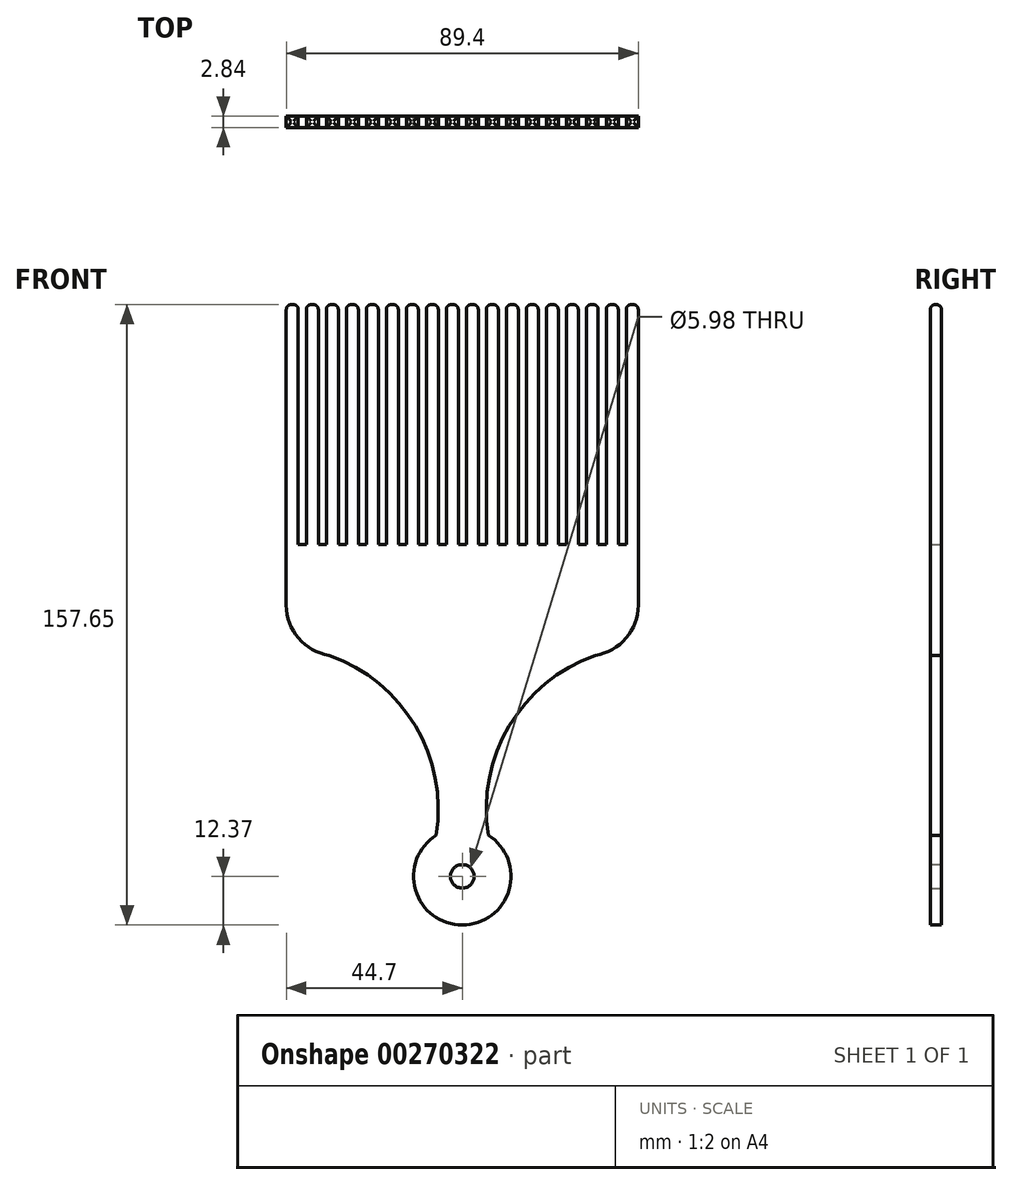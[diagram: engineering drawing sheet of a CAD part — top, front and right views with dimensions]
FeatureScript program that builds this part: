
annotation { "Feature Type Name" : "Feature", "Feature Type Description" : "" }
export const myFeature = defineFeature(function(context is Context, id is Id, definition is map)
    precondition{}
    {
        {
            var Q0;
            Q0=qCreatedBy(makeId("Front.planeOp"),FACE);
            var sketch = newSketch(context, id + "F0", { "sketchPlane" : qUnion([Q0])});
            skLineSegment(sketch, "E0", {"start": v(-55.88, 181.6) * mm, "end": v(-55.88, 86.13) * mm});
            skLineSegment(sketch, "E1", {"start": v(-55.88, 181.6) * mm, "end": v(-52.07, 181.6) * mm});
            skLineSegment(sketch, "E2", {"start": v(-52.07, 181.6) * mm, "end": v(-52.07, 105.4) * mm});
            skArc(sketch, "E3", {"start": v(-55.88, 86.13) * mm, "mid": v(-52, 75.65) * mm, "end": v(-42.24, 70.21) * mm});
            skArc(sketch, "E4", {"start": v(-8.28, 13.06) * mm, "mid": v(-14.9, 47.8) * mm, "end": v(-42.24, 70.21) * mm});
            skArc(sketch, "E5", {"start": v(-8.28, 13.06) * mm, "mid": v(-14.86, -4.31) * mm, "end": v(0, -15.47) * mm});
            skLineSegment(sketch, "E6", {"start": v(-52.07, 105.4) * mm, "end": v(-49.53, 105.4) * mm});
            skLineSegment(sketch, "E7", {"start": v(-49.53, 105.4) * mm, "end": v(-49.53, 181.6) * mm});
            skLineSegment(sketch, "E8", {"start": v(-49.53, 181.6) * mm, "end": v(-45.72, 181.6) * mm});
            skLineSegment(sketch, "E9", {"start": v(-45.72, 181.6) * mm, "end": v(-45.72, 105.4) * mm});
            skLineSegment(sketch, "E10", {"start": v(-45.72, 105.4) * mm, "end": v(-43.18, 105.4) * mm});
            skLineSegment(sketch, "E11", {"start": v(0, -168.17) * mm, "end": v(0, 92.35) * mm, "construction": true});
            skLineSegment(sketch, "E12.MirrorCS", {"start": v(55.88, 181.6) * mm, "end": v(52.07, 181.6) * mm});
            skLineSegment(sketch, "E13.MirrorCS", {"start": v(49.53, 181.6) * mm, "end": v(45.72, 181.6) * mm});
            skLineSegment(sketch, "E14.MirrorCS", {"start": v(45.72, 105.4) * mm, "end": v(43.18, 105.4) * mm});
            skLineSegment(sketch, "E15.MirrorCS", {"start": v(52.07, 105.4) * mm, "end": v(49.53, 105.4) * mm});
            skLineSegment(sketch, "E16.MirrorCS", {"start": v(52.07, 181.6) * mm, "end": v(52.07, 105.4) * mm});
            skArc(sketch, "E17.MirrorCS", {"start": v(8.28, 13.06) * mm, "mid": v(14.86, -4.31) * mm, "end": v(0, -15.47) * mm});
            skLineSegment(sketch, "E18.MirrorCS", {"start": v(45.72, 181.6) * mm, "end": v(45.72, 105.4) * mm});
            skArc(sketch, "E19.MirrorCS", {"start": v(55.88, 86.13) * mm, "mid": v(52, 75.65) * mm, "end": v(42.24, 70.21) * mm});
            skLineSegment(sketch, "E20.MirrorCS", {"start": v(49.53, 105.4) * mm, "end": v(49.53, 181.6) * mm});
            skArc(sketch, "E21.MirrorCS", {"start": v(8.28, 13.06) * mm, "mid": v(14.9, 47.8) * mm, "end": v(42.24, 70.21) * mm});
            skLineSegment(sketch, "E22.MirrorCS", {"start": v(55.88, 181.6) * mm, "end": v(55.88, 86.13) * mm});
            skLineSegment(sketch, "E23.1.0.0", {"start": v(-39.37, 181.6) * mm, "end": v(-39.37, 105.4) * mm});
            skLineSegment(sketch, "E23.1.0.1", {"start": v(-43.18, 105.4) * mm, "end": v(-43.18, 181.6) * mm});
            skLineSegment(sketch, "E23.1.0.2", {"start": v(-39.37, 105.4) * mm, "end": v(-36.83, 105.4) * mm});
            skLineSegment(sketch, "E23.1.0.3", {"start": v(-43.18, 181.6) * mm, "end": v(-39.37, 181.6) * mm});
            skLineSegment(sketch, "E23.2.0.0", {"start": v(-33.02, 181.6) * mm, "end": v(-33.02, 105.4) * mm});
            skLineSegment(sketch, "E23.2.0.1", {"start": v(-36.83, 105.4) * mm, "end": v(-36.83, 181.6) * mm});
            skLineSegment(sketch, "E23.2.0.2", {"start": v(-33.02, 105.4) * mm, "end": v(-30.48, 105.4) * mm});
            skLineSegment(sketch, "E23.2.0.3", {"start": v(-36.83, 181.6) * mm, "end": v(-33.02, 181.6) * mm});
            skLineSegment(sketch, "E23.3.0.0", {"start": v(-26.67, 181.6) * mm, "end": v(-26.67, 105.4) * mm});
            skLineSegment(sketch, "E23.3.0.1", {"start": v(-30.48, 105.4) * mm, "end": v(-30.48, 181.6) * mm});
            skLineSegment(sketch, "E23.3.0.2", {"start": v(-26.67, 105.4) * mm, "end": v(-24.13, 105.4) * mm});
            skLineSegment(sketch, "E23.3.0.3", {"start": v(-30.48, 181.6) * mm, "end": v(-26.67, 181.6) * mm});
            skLineSegment(sketch, "E23.4.0.0", {"start": v(-20.32, 181.6) * mm, "end": v(-20.32, 105.4) * mm});
            skLineSegment(sketch, "E23.4.0.1", {"start": v(-24.13, 105.4) * mm, "end": v(-24.13, 181.6) * mm});
            skLineSegment(sketch, "E23.4.0.2", {"start": v(-20.32, 105.4) * mm, "end": v(-17.78, 105.4) * mm});
            skLineSegment(sketch, "E23.4.0.3", {"start": v(-24.13, 181.6) * mm, "end": v(-20.32, 181.6) * mm});
            skLineSegment(sketch, "E23.5.0.0", {"start": v(-13.97, 181.6) * mm, "end": v(-13.97, 105.4) * mm});
            skLineSegment(sketch, "E23.5.0.1", {"start": v(-17.78, 105.4) * mm, "end": v(-17.78, 181.6) * mm});
            skLineSegment(sketch, "E23.5.0.2", {"start": v(-13.97, 105.4) * mm, "end": v(-11.43, 105.4) * mm});
            skLineSegment(sketch, "E23.5.0.3", {"start": v(-17.78, 181.6) * mm, "end": v(-13.97, 181.6) * mm});
            skLineSegment(sketch, "E23.6.0.0", {"start": v(-7.62, 181.6) * mm, "end": v(-7.62, 105.4) * mm});
            skLineSegment(sketch, "E23.6.0.1", {"start": v(-11.43, 105.4) * mm, "end": v(-11.43, 181.6) * mm});
            skLineSegment(sketch, "E23.6.0.2", {"start": v(-7.62, 105.4) * mm, "end": v(-5.08, 105.4) * mm});
            skLineSegment(sketch, "E23.6.0.3", {"start": v(-11.43, 181.6) * mm, "end": v(-7.62, 181.6) * mm});
            skLineSegment(sketch, "E23.7.0.0", {"start": v(-1.27, 181.6) * mm, "end": v(-1.27, 105.4) * mm});
            skLineSegment(sketch, "E23.7.0.1", {"start": v(-5.08, 105.4) * mm, "end": v(-5.08, 181.6) * mm});
            skLineSegment(sketch, "E23.7.0.2", {"start": v(-1.27, 105.4) * mm, "end": v(1.27, 105.4) * mm});
            skLineSegment(sketch, "E23.7.0.3", {"start": v(-5.08, 181.6) * mm, "end": v(-1.27, 181.6) * mm});
            skLineSegment(sketch, "E23.direction1", {"start": v(-49.53, 105.4) * mm, "end": v(-43.18, 105.4) * mm, "construction": true});
            skLineSegment(sketch, "E24.MirrorCS", {"start": v(11.43, 181.6) * mm, "end": v(7.62, 181.6) * mm});
            skLineSegment(sketch, "E25.MirrorCS", {"start": v(20.32, 105.4) * mm, "end": v(17.78, 105.4) * mm});
            skLineSegment(sketch, "E26.MirrorCS", {"start": v(7.62, 105.4) * mm, "end": v(5.08, 105.4) * mm});
            skLineSegment(sketch, "E27.MirrorCS", {"start": v(17.78, 181.6) * mm, "end": v(13.97, 181.6) * mm});
            skLineSegment(sketch, "E28.MirrorCS", {"start": v(30.48, 181.6) * mm, "end": v(26.67, 181.6) * mm});
            skLineSegment(sketch, "E29.MirrorCS", {"start": v(26.67, 105.4) * mm, "end": v(24.13, 105.4) * mm});
            skLineSegment(sketch, "E30.MirrorCS", {"start": v(13.97, 105.4) * mm, "end": v(11.43, 105.4) * mm});
            skLineSegment(sketch, "E31.MirrorCS", {"start": v(24.13, 181.6) * mm, "end": v(20.32, 181.6) * mm});
            skLineSegment(sketch, "E32.MirrorCS", {"start": v(39.37, 105.4) * mm, "end": v(36.83, 105.4) * mm});
            skLineSegment(sketch, "E33.MirrorCS", {"start": v(33.02, 105.4) * mm, "end": v(30.48, 105.4) * mm});
            skLineSegment(sketch, "E34.MirrorCS", {"start": v(5.08, 181.6) * mm, "end": v(1.27, 181.6) * mm});
            skLineSegment(sketch, "E35.MirrorCS", {"start": v(1.27, 105.4) * mm, "end": v(-1.27, 105.4) * mm});
            skLineSegment(sketch, "E36.MirrorCS", {"start": v(1.27, 181.6) * mm, "end": v(1.27, 105.4) * mm});
            skLineSegment(sketch, "E37.MirrorCS", {"start": v(17.78, 105.4) * mm, "end": v(17.78, 181.6) * mm});
            skLineSegment(sketch, "E38.MirrorCS", {"start": v(36.83, 181.6) * mm, "end": v(33.02, 181.6) * mm});
            skLineSegment(sketch, "E39.MirrorCS", {"start": v(5.08, 105.4) * mm, "end": v(5.08, 181.6) * mm});
            skLineSegment(sketch, "E40.MirrorCS", {"start": v(26.67, 181.6) * mm, "end": v(26.67, 105.4) * mm});
            skLineSegment(sketch, "E41.MirrorCS", {"start": v(39.37, 181.6) * mm, "end": v(39.37, 105.4) * mm});
            skLineSegment(sketch, "E42.MirrorCS", {"start": v(13.97, 181.6) * mm, "end": v(13.97, 105.4) * mm});
            skLineSegment(sketch, "E43.MirrorCS", {"start": v(43.18, 105.4) * mm, "end": v(43.18, 181.6) * mm});
            skLineSegment(sketch, "E44.MirrorCS", {"start": v(30.48, 105.4) * mm, "end": v(30.48, 181.6) * mm});
            skLineSegment(sketch, "E45.MirrorCS", {"start": v(43.18, 181.6) * mm, "end": v(39.37, 181.6) * mm});
            skLineSegment(sketch, "E46.MirrorCS", {"start": v(49.53, 105.4) * mm, "end": v(43.18, 105.4) * mm, "construction": true});
            skLineSegment(sketch, "E47.MirrorCS", {"start": v(11.43, 105.4) * mm, "end": v(11.43, 181.6) * mm});
            skLineSegment(sketch, "E48.MirrorCS", {"start": v(33.02, 181.6) * mm, "end": v(33.02, 105.4) * mm});
            skLineSegment(sketch, "E49.MirrorCS", {"start": v(36.83, 105.4) * mm, "end": v(36.83, 181.6) * mm});
            skLineSegment(sketch, "E50.MirrorCS", {"start": v(24.13, 105.4) * mm, "end": v(24.13, 181.6) * mm});
            skLineSegment(sketch, "E51.MirrorCS", {"start": v(7.62, 181.6) * mm, "end": v(7.62, 105.4) * mm});
            skLineSegment(sketch, "E52.MirrorCS", {"start": v(20.32, 181.6) * mm, "end": v(20.32, 105.4) * mm});
            skCircle(sketch, "E53", {"center": v(0, 0) * mm, "radius": 3.74 * mm});
            skSolve(sketch);
        }
        {
            var Q0;
            Q0 = qSketchRegion(id + "F0", true);
            extrude(context, id + "F1", {"entities" : qUnion([Q0]), "depth" : 3.56 * mm});
        }
        {
            var Q0;
            Q0=qCreatedBy(makeId("Front.planeOp"),FACE);
            cPlane(context, id + "F2", {"entities" : qUnion([Q0]), "cplaneType" : CPlaneType.OFFSET, "offset" : 1.27 * mm, "width" : 152.4 * mm, "height" : 152.4 * mm});
        }
        {
            var Q0;
            Q0=makeQuery(id+"F1.opExtrude","SWEPT_BODY",BODY,{"disambiguationData":[OSD([sQuery(id+"F0.wireOp",EDGE,"E0"),sQuery(id+"F0.wireOp",EDGE,"E1"),sQuery(id+"F0.wireOp",EDGE,"E2"),sQuery(id+"F0.wireOp",EDGE,"E3"),sQuery(id+"F0.wireOp",EDGE,"E4"),sQuery(id+"F0.wireOp",EDGE,"E5"),sQuery(id+"F0.wireOp",EDGE,"E6"),sQuery(id+"F0.wireOp",EDGE,"E7"),sQuery(id+"F0.wireOp",EDGE,"E8"),sQuery(id+"F0.wireOp",EDGE,"E9"),sQuery(id+"F0.wireOp",EDGE,"E10"),sQuery(id+"F0.wireOp",EDGE,"E12.MirrorCS"),sQuery(id+"F0.wireOp",EDGE,"E15.MirrorCS"),sQuery(id+"F0.wireOp",EDGE,"E16.MirrorCS"),sQuery(id+"F0.wireOp",EDGE,"E17.MirrorCS"),sQuery(id+"F0.wireOp",EDGE,"E19.MirrorCS"),sQuery(id+"F0.wireOp",EDGE,"E21.MirrorCS"),sQuery(id+"F0.wireOp",EDGE,"E22.MirrorCS"),sQuery(id+"F0.wireOp",EDGE,"E23.1.0.0"),sQuery(id+"F0.wireOp",EDGE,"E23.1.0.1"),sQuery(id+"F0.wireOp",EDGE,"E23.1.0.2"),sQuery(id+"F0.wireOp",EDGE,"E23.1.0.3"),sQuery(id+"F0.wireOp",EDGE,"E23.2.0.0"),sQuery(id+"F0.wireOp",EDGE,"E23.2.0.1"),sQuery(id+"F0.wireOp",EDGE,"E23.2.0.2"),sQuery(id+"F0.wireOp",EDGE,"E23.2.0.3"),sQuery(id+"F0.wireOp",EDGE,"E23.3.0.0"),sQuery(id+"F0.wireOp",EDGE,"E23.3.0.1"),sQuery(id+"F0.wireOp",EDGE,"E23.3.0.2"),sQuery(id+"F0.wireOp",EDGE,"E23.3.0.3"),sQuery(id+"F0.wireOp",EDGE,"E23.4.0.0"),sQuery(id+"F0.wireOp",EDGE,"E23.4.0.1"),sQuery(id+"F0.wireOp",EDGE,"E23.4.0.2"),sQuery(id+"F0.wireOp",EDGE,"E23.4.0.3"),sQuery(id+"F0.wireOp",EDGE,"E23.5.0.0"),sQuery(id+"F0.wireOp",EDGE,"E23.5.0.1"),sQuery(id+"F0.wireOp",EDGE,"E23.5.0.2"),sQuery(id+"F0.wireOp",EDGE,"E23.5.0.3"),sQuery(id+"F0.wireOp",EDGE,"E23.6.0.0"),sQuery(id+"F0.wireOp",EDGE,"E23.6.0.1"),sQuery(id+"F0.wireOp",EDGE,"E23.6.0.2"),sQuery(id+"F0.wireOp",EDGE,"E23.6.0.3"),sQuery(id+"F0.wireOp",EDGE,"E23.7.0.0"),sQuery(id+"F0.wireOp",EDGE,"E23.7.0.1"),sQuery(id+"F0.wireOp",EDGE,"E23.7.0.3"),sQuery(id+"F0.wireOp",EDGE,"E14.MirrorCS"),sQuery(id+"F0.wireOp",EDGE,"E24.MirrorCS"),sQuery(id+"F0.wireOp",EDGE,"E25.MirrorCS"),sQuery(id+"F0.wireOp",EDGE,"E26.MirrorCS"),sQuery(id+"F0.wireOp",EDGE,"E27.MirrorCS"),sQuery(id+"F0.wireOp",EDGE,"E28.MirrorCS"),sQuery(id+"F0.wireOp",EDGE,"E29.MirrorCS"),sQuery(id+"F0.wireOp",EDGE,"E30.MirrorCS"),sQuery(id+"F0.wireOp",EDGE,"E31.MirrorCS"),sQuery(id+"F0.wireOp",EDGE,"E32.MirrorCS"),sQuery(id+"F0.wireOp",EDGE,"E33.MirrorCS"),sQuery(id+"F0.wireOp",EDGE,"E34.MirrorCS"),sQuery(id+"F0.wireOp",EDGE,"E35.MirrorCS"),sQuery(id+"F0.wireOp",EDGE,"E18.MirrorCS"),sQuery(id+"F0.wireOp",EDGE,"E20.MirrorCS"),sQuery(id+"F0.wireOp",EDGE,"E13.MirrorCS"),sQuery(id+"F0.wireOp",EDGE,"E36.MirrorCS"),sQuery(id+"F0.wireOp",EDGE,"E37.MirrorCS"),sQuery(id+"F0.wireOp",EDGE,"E38.MirrorCS"),sQuery(id+"F0.wireOp",EDGE,"E39.MirrorCS"),sQuery(id+"F0.wireOp",EDGE,"E40.MirrorCS"),sQuery(id+"F0.wireOp",EDGE,"E41.MirrorCS"),sQuery(id+"F0.wireOp",EDGE,"E42.MirrorCS"),sQuery(id+"F0.wireOp",EDGE,"E43.MirrorCS"),sQuery(id+"F0.wireOp",EDGE,"E44.MirrorCS"),sQuery(id+"F0.wireOp",EDGE,"E45.MirrorCS"),sQuery(id+"F0.wireOp",EDGE,"E47.MirrorCS"),sQuery(id+"F0.wireOp",EDGE,"E48.MirrorCS"),sQuery(id+"F0.wireOp",EDGE,"E49.MirrorCS"),sQuery(id+"F0.wireOp",EDGE,"E50.MirrorCS"),sQuery(id+"F0.wireOp",EDGE,"E51.MirrorCS"),sQuery(id+"F0.wireOp",EDGE,"E52.MirrorCS"),sQuery(id+"F0.wireOp",EDGE,"E53")])]});
            var Q1;
            Q1=sQuery(id+"F0.wireOp",VERTEX,"E53.center");
            transform(context, id + "F3", {"entities" : qUnion([Q0]), "transformType" : TransformType.SCALE_UNIFORMLY, "scale" : .8, "scalePoint" : qUnion([Q1]), "makeCopy" : false});
        }
        {
            var Q0;
            Q0=makeQuery(id+"F1.opExtrude","CAP_EDGE",EDGE,{"disambiguationData":[OSD([sQuery(id+"F0.wireOp",EDGE,"E45.MirrorCS")])],"isStart":false});
            var Q1;
            Q1=makeQuery(id+"F1.opExtrude","CAP_EDGE",EDGE,{"disambiguationData":[OSD([sQuery(id+"F0.wireOp",EDGE,"E45.MirrorCS")])],"isStart":true});
            var Q2;
            Q2=makeQuery(id+"F1.opExtrude","SWEPT_EDGE",EDGE,{"disambiguationData":[OSD([sQuery(id+"F0.wireOp",EDGE,"E41.MirrorCS"),sQuery(id+"F0.wireOp",EDGE,"E45.MirrorCS")])]});
            var Q3;
            Q3=makeQuery(id+"F1.opExtrude","SWEPT_EDGE",EDGE,{"disambiguationData":[OSD([sQuery(id+"F0.wireOp",EDGE,"E43.MirrorCS"),sQuery(id+"F0.wireOp",EDGE,"E45.MirrorCS")])]});
            var Q4;
            Q4=makeQuery(id+"F1.opExtrude","SWEPT_FACE",FACE,{"disambiguationData":[OSD([sQuery(id+"F0.wireOp",EDGE,"E13.MirrorCS")])]});
            var Q5;
            Q5=makeQuery(id+"F1.opExtrude","SWEPT_FACE",FACE,{"disambiguationData":[OSD([sQuery(id+"F0.wireOp",EDGE,"E12.MirrorCS")])]});
            var Q6;
            Q6=makeQuery(id+"F1.opExtrude","SWEPT_FACE",FACE,{"disambiguationData":[OSD([sQuery(id+"F0.wireOp",EDGE,"E38.MirrorCS")])]});
            var Q7;
            Q7=makeQuery(id+"F1.opExtrude","SWEPT_FACE",FACE,{"disambiguationData":[OSD([sQuery(id+"F0.wireOp",EDGE,"E28.MirrorCS")])]});
            var Q8;
            Q8=makeQuery(id+"F1.opExtrude","SWEPT_FACE",FACE,{"disambiguationData":[OSD([sQuery(id+"F0.wireOp",EDGE,"E31.MirrorCS")])]});
            var Q9;
            Q9=makeQuery(id+"F1.opExtrude","SWEPT_FACE",FACE,{"disambiguationData":[OSD([sQuery(id+"F0.wireOp",EDGE,"E27.MirrorCS")])]});
            var Q10;
            Q10=makeQuery(id+"F1.opExtrude","SWEPT_FACE",FACE,{"disambiguationData":[OSD([sQuery(id+"F0.wireOp",EDGE,"E24.MirrorCS")])]});
            var Q11;
            Q11=makeQuery(id+"F1.opExtrude","SWEPT_FACE",FACE,{"disambiguationData":[OSD([sQuery(id+"F0.wireOp",EDGE,"E34.MirrorCS")])]});
            var Q12;
            Q12=makeQuery(id+"F1.opExtrude","SWEPT_FACE",FACE,{"disambiguationData":[OSD([sQuery(id+"F0.wireOp",EDGE,"E23.7.0.3")])]});
            var Q13;
            Q13=makeQuery(id+"F1.opExtrude","SWEPT_FACE",FACE,{"disambiguationData":[OSD([sQuery(id+"F0.wireOp",EDGE,"E23.6.0.3")])]});
            var Q14;
            Q14=makeQuery(id+"F1.opExtrude","SWEPT_FACE",FACE,{"disambiguationData":[OSD([sQuery(id+"F0.wireOp",EDGE,"E23.5.0.3")])]});
            var Q15;
            Q15=makeQuery(id+"F1.opExtrude","SWEPT_FACE",FACE,{"disambiguationData":[OSD([sQuery(id+"F0.wireOp",EDGE,"E23.4.0.3")])]});
            var Q16;
            Q16=makeQuery(id+"F1.opExtrude","SWEPT_FACE",FACE,{"disambiguationData":[OSD([sQuery(id+"F0.wireOp",EDGE,"E23.3.0.3")])]});
            var Q17;
            Q17=makeQuery(id+"F1.opExtrude","SWEPT_FACE",FACE,{"disambiguationData":[OSD([sQuery(id+"F0.wireOp",EDGE,"E23.2.0.3")])]});
            var Q18;
            Q18=makeQuery(id+"F1.opExtrude","SWEPT_FACE",FACE,{"disambiguationData":[OSD([sQuery(id+"F0.wireOp",EDGE,"E23.1.0.3")])]});
            var Q19;
            Q19=makeQuery(id+"F1.opExtrude","SWEPT_FACE",FACE,{"disambiguationData":[OSD([sQuery(id+"F0.wireOp",EDGE,"E8")])]});
            var Q20;
            Q20=makeQuery(id+"F1.opExtrude","SWEPT_FACE",FACE,{"disambiguationData":[OSD([sQuery(id+"F0.wireOp",EDGE,"E1")])]});
            fillet(context, id + "F4", {"entities" : qUnion([Q0, Q1, Q2, Q3, Q4, Q5, Q6, Q7, Q8, Q9, Q10, Q11, Q12, Q13, Q14, Q15, Q16, Q17, Q18, Q19, Q20]), "radius" : 1.27 * mm, "tangentPropagation" : true, "allowEdgeOverflow" : false});
        }
    });
